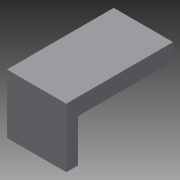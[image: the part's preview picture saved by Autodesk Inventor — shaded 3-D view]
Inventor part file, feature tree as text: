
AUTODESK INVENTOR PART (.ipt)
format: ipt  version: 2015 (Build 190159000, 159)  size: 77,824 bytes
history: native  units: mm
features: extrude x2, sketch x2
ambient origin geometry x8: Origin, YZ Plane, XZ Plane, XY Plane, X Axis, Y Axis, Z Axis, Center Point
bodies: Solid1 (feature_tree)
feature tree (4):
  extrude  "Extrusion1"  Depth=25.0mm
  extrude  "Extrusion2"  Depth=7.0mm
  sketch  "Sketch1"  dims[d0=25.0mm d1=25.0mm]
  sketch  "Sketch2"  dims[d2=5.0mm d3=0.0mm d4=7.0mm d5=40.0mm d6=0.0mm]
